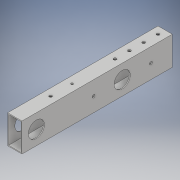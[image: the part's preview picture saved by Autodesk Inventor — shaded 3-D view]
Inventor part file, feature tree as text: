
AUTODESK INVENTOR PART (.ipt)
format: ipt  version: 2018 (Build 220112000, 112)  size: 160,768 bytes
history: native  units: in
note: dims shown in document units (in); Inventor stores cm internally (conversion verified against a paired STEP export)
features: extrude x7, sketch x7
ambient origin geometry x8: Origin, YZ Plane, XZ Plane, XY Plane, X Axis, Y Axis, Z Axis, Center Point
bodies: Solid1 (feature_tree)
feature tree (14):
  extrude  "Extrusion1"  Depth=2.0in
  sketch  "Sketch2"  dims[d2=0.0625in d3=10.5in d4=0.0in]
  extrude  "Extrusion4"  Depth=10.5in TaperAngle=0.0deg
  extrude  "Extrusion5"  Depth=1.0in
  extrude  "Extrusion7"  Depth=1.0in
  extrude  "Extrusion8"  Depth=1.0in
  extrude  "Extrusion9"  Depth=1.0in TaperAngle=0.0deg
  extrude  "Extrusion10"  TaperAngle=180.0deg  [1 undecoded]
  sketch  "Sketch1"  dims[d0=1.0in d1=2.0in]
  sketch  "Sketch4"  dims[d14=0.5in d15=1.0in]
  sketch  "Sketch5"  dims[d16=1.0in d17=0.2031in]
  sketch  "Sketch6"  dims[d18=2.6875in d19=0.0in d20=1.0in]
  sketch  "Sketch7"  dims[d21=1.125in d22=1.0in d23=0.0in]
  sketch  "Sketch8"  dims[d24=1.5in d25=180.0deg d26=4.0in d27=0.2031in d30=1.125in d31=1.0in d32=0.0in d33=6.5in d34=0.156in d35=2.625in d36=0.0in d37=1.0in d38=2.625in d39=0.0in d40=2.5in d41=0.2031in d42=2.625in d43=0.0in]
note: 1 required parameter value undecoded (feature->parameter linkage not recoverable at this tier; creation-order binding heuristic only, values carry confidence <= 0.55)
